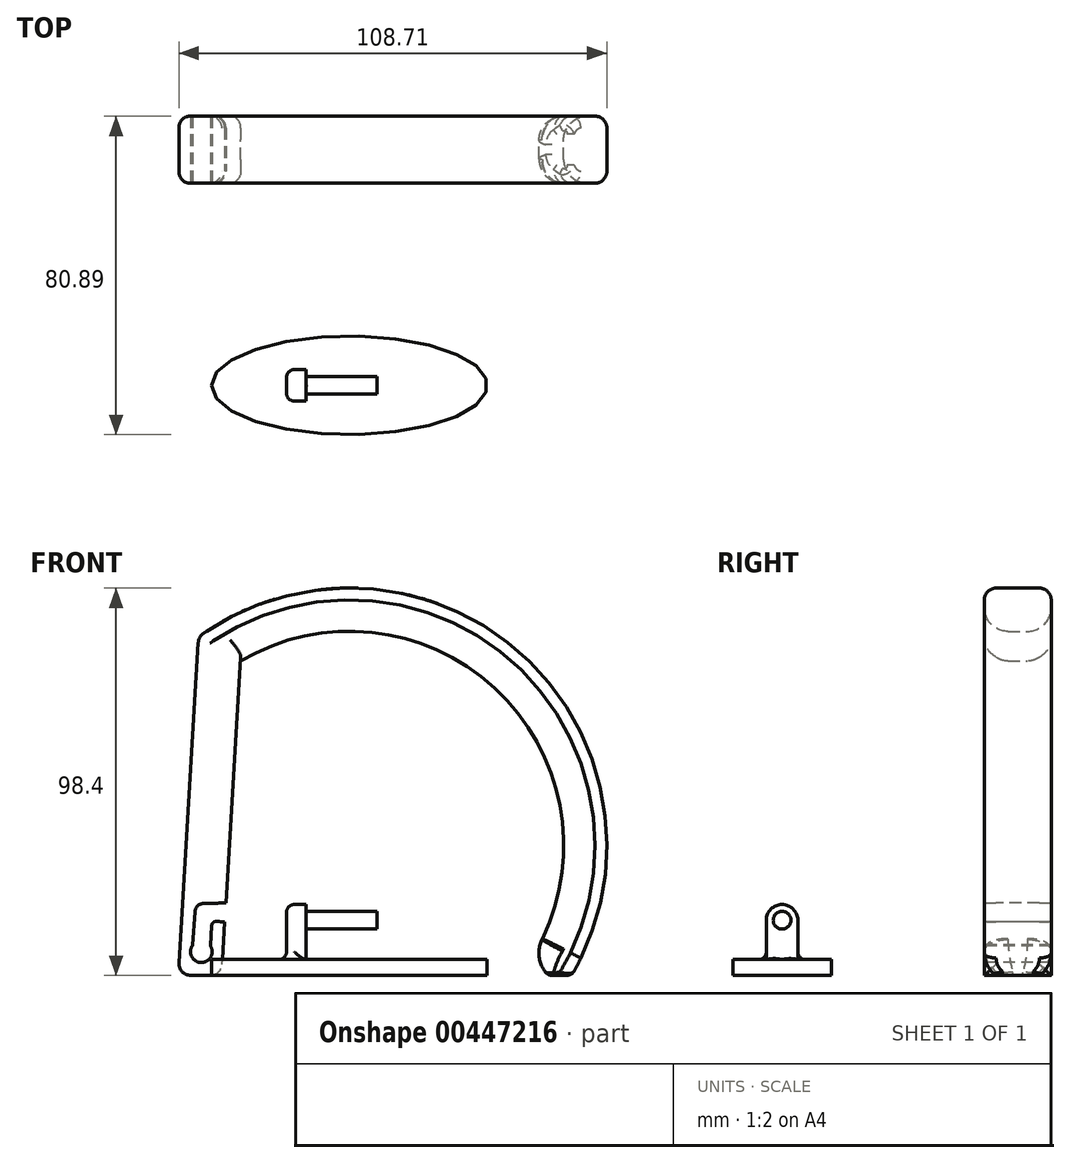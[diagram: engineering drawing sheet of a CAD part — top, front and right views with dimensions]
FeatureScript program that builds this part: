
annotation { "Feature Type Name" : "Feature", "Feature Type Description" : "" }
export const myFeature = defineFeature(function(context is Context, id is Id, definition is map)
    precondition{}
    {
        {
            var Q0;
            Q0=qCreatedBy(makeId("Front.planeOp"),FACE);
            var sketch = newSketch(context, id + "F0", { "sketchPlane" : qUnion([Q0])});
            skArc(sketch, "E0", {"start": v(50, 0) * mm, "mid": v(42.36, 75.36) * mm, "end": v(-33, 83) * mm});
            skLineSegment(sketch, "E1", {"start": v(-38, 0) * mm, "end": v(-33, 83) * mm});
            skArc(sketch, "E2", {"start": v(-33, 83) * mm, "mid": v(-58.69, 45.02) * mm, "end": v(-50, 0) * mm});
            skSolve(sketch);
        }
        {
            var Q0;
            Q0=qCreatedBy(makeId("Top.planeOp"),FACE);
            var sketch = newSketch(context, id + "F1", { "sketchPlane" : qUnion([Q0])});
            skLineSegment(sketch, "E3.bottom", {"start": v(-32.5, 8.5) * mm, "end": v(-43.5, 8.5) * mm});
            skLineSegment(sketch, "E3.top", {"start": v(-32.5, -8.5) * mm, "end": v(-43.5, -8.5) * mm});
            skLineSegment(sketch, "E3.left", {"start": v(-32.5, 8.5) * mm, "end": v(-32.5, -8.5) * mm});
            skLineSegment(sketch, "E3.right", {"start": v(-43.5, 8.5) * mm, "end": v(-43.5, -8.5) * mm});
            skPoint(sketch, "E3.middle", {"position": v(-38, 0) * mm});
            skSolve(sketch);
        }
        {
            var Q0;
            Q0=makeQuery(id+"F1.imprint","IMPRINT",FACE,{"disambiguationData":[TD([[makeQuery(id+"F1.imprint","IMPRINT",EDGE,{"derivedFrom":sQuery(id+"F1.wireOp",EDGE,"E3.bottom")}),1.0]])]});
            var Q1;
            Q1=sQuery(id+"F0.wireOp",EDGE,"E0");
            var Q2;
            Q2=sQuery(id+"F0.wireOp",EDGE,"E1");
            sweep(context, id + "F2", {"profiles" : qUnion([Q0]), "path" : qUnion([Q1, Q2])});
        }
        {
            var Q0;
            Q0=makeQuery(id+"F2.opSweep","SWEPT_FACE",FACE,{"disambiguationData":[OSD([sQuery(id+"F0.wireOp",EDGE,"E0"),sQuery(id+"F1.wireOp",EDGE,"E3.right")])]});
            var Q1;
            Q1=makeQuery(id+"F2.opSweep","SWEPT_FACE",FACE,{"disambiguationData":[OSD([sQuery(id+"F0.wireOp",EDGE,"E1"),sQuery(id+"F1.wireOp",EDGE,"E3.right")])]});
            var Q2;
            Q2=makeQuery(id+"F2.opSweep","SWEPT_EDGE",EDGE,{"disambiguationData":[OSD([sQuery(id+"F0.wireOp",EDGE,"E1"),sQuery(id+"F1.wireOp",EDGE,"E3.top"),sQuery(id+"F1.wireOp",EDGE,"E3.left")])]});
            var Q3;
            Q3=makeQuery(id+"F2.opSweep","SWEPT_EDGE",EDGE,{"disambiguationData":[OSD([sQuery(id+"F0.wireOp",EDGE,"E1"),sQuery(id+"F1.wireOp",EDGE,"E3.bottom"),sQuery(id+"F1.wireOp",EDGE,"E3.left")])]});
            var Q4;
            Q4=makeQuery(id+"F2.opSweep","CAP_EDGE",EDGE,{"disambiguationData":[OSD([sQuery(id+"F0.wireOp",VERTEX,"E1.start"),sQuery(id+"F1.wireOp",EDGE,"E3.left")])],"isStart":true});
            fillet(context, id + "F3", {"entities" : qUnion([Q0, Q1, Q2, Q3, Q4]), "radius" : 3 * mm, "tangentPropagation" : true, "allowEdgeOverflow" : false});
        }
        {
            var Q0;
            Q0=qCreatedBy(makeId("Front.planeOp"),FACE);
            var sketch = newSketch(context, id + "F4", { "sketchPlane" : qUnion([Q0])});
            skPoint(sketch, "E4", {"position": v(-37.64, 6) * mm});
            skPoint(sketch, "E5", {"position": v(-37.04, 16) * mm});
            skPoint(sketch, "E6", {"position": v(-27.04, 16) * mm});
            skCircle(sketch, "E7", {"center": v(-27.04, 16) * mm, "radius": 2.5 * mm});
            skCircle(sketch, "E8", {"center": v(-37.04, 16) * mm, "radius": 2.25 * mm});
            skCircle(sketch, "E9", {"center": v(-37.64, 6) * mm, "radius": 2.25 * mm});
            skLineSegment(sketch, "E10", {"start": v(-35.4, 5.86) * mm, "end": v(-34.8, 15.86) * mm});
            skLineSegment(sketch, "E11", {"start": v(-39.88, 6.14) * mm, "end": v(-39.28, 16.14) * mm});
            skLineSegment(sketch, "E12", {"start": v(-27.1, 18.5) * mm, "end": v(-37.1, 18.25) * mm});
            skLineSegment(sketch, "E13", {"start": v(-27.1, 13.5) * mm, "end": v(-37.1, 13.75) * mm});
            skCircle(sketch, "E14", {"center": v(-37.64, 6) * mm, "radius": 2.75 * mm});
            skSolve(sketch);
        }
        {
            var Q0;
            {var subQ0=sQuery(id+"F4.wireOp",EDGE,"E7");var subQ1=makeQuery(id+"F4.imprint","INTERSECT",VERTEX,{"derivedFrom":[subQ0,sQuery(id+"F4.wireOp",EDGE,"E12")]});Q0=makeQuery(id+"F4.imprint","IMPRINT",FACE,{"disambiguationData":[TD([[makeQuery(id+"F4.imprint","IMPRINT",EDGE,{"disambiguationData":[TD([[subQ1,-1.0]])],"derivedFrom":subQ0}),1.0]])]});}
            var Q1;
            {var subQ0=sQuery(id+"F4.wireOp",EDGE,"E12");Q1=makeQuery(id+"F4.imprint","IMPRINT",FACE,{"disambiguationData":[TD([[makeQuery(id+"F4.imprint","IMPRINT",EDGE,{"derivedFrom":subQ0}),1.0]])]});}
            var Q2;
            {var subQ0=sQuery(id+"F4.wireOp",EDGE,"E8");var subQ1=makeQuery(id+"F4.imprint","INTERSECT",VERTEX,{"derivedFrom":[subQ0,sQuery(id+"F4.wireOp",EDGE,"E10")]});Q2=makeQuery(id+"F4.imprint","IMPRINT",FACE,{"disambiguationData":[TD([[makeQuery(id+"F4.imprint","IMPRINT",EDGE,{"disambiguationData":[TD([[subQ1,-1.0]])],"derivedFrom":subQ0}),1.0]])]});}
            var Q3;
            {var subQ1=sQuery(id+"F4.wireOp",EDGE,"E8");var subQ5=sQuery(id+"F4.wireOp",EDGE,"E11");var subQ6=makeQuery(id+"F4.imprint","INTERSECT",VERTEX,{"derivedFrom":[subQ1,subQ5]});Q3=makeQuery(id+"F4.imprint","IMPRINT",FACE,{"disambiguationData":[TD([[makeQuery(id+"F4.imprint","IMPRINT",EDGE,{"disambiguationData":[TD([[subQ6,-1.0]])],"derivedFrom":subQ1}),-1.0]])]});}
            var Q4;
            {var subQ0=sQuery(id+"F4.wireOp",EDGE,"E10");var subQ1=sQuery(id+"F4.wireOp",EDGE,"E8");var subQ2=makeQuery(id+"F4.imprint","INTERSECT",VERTEX,{"derivedFrom":[subQ1,subQ0]});Q4=makeQuery(id+"F4.imprint","IMPRINT",FACE,{"disambiguationData":[TD([[makeQuery(id+"F4.imprint","IMPRINT",EDGE,{"disambiguationData":[TD([[subQ2,1.0]])],"derivedFrom":subQ1}),-1.0]])]});}
            var Q5;
            {var subQ0=sQuery(id+"F4.wireOp",EDGE,"E10");var subQ1=sQuery(id+"F4.wireOp",EDGE,"E9");var subQ2=makeQuery(id+"F4.imprint","INTERSECT",VERTEX,{"derivedFrom":[subQ1,subQ0]});Q5=makeQuery(id+"F4.imprint","IMPRINT",FACE,{"disambiguationData":[TD([[makeQuery(id+"F4.imprint","IMPRINT",EDGE,{"disambiguationData":[TD([[subQ2,-1.0]])],"derivedFrom":subQ1}),-1.0]])]});}
            var Q6;
            {var subQ0=sQuery(id+"F4.wireOp",EDGE,"E10");var subQ1=sQuery(id+"F4.wireOp",EDGE,"E9");var subQ2=makeQuery(id+"F4.imprint","INTERSECT",VERTEX,{"derivedFrom":[subQ1,subQ0]});Q6=makeQuery(id+"F4.imprint","IMPRINT",FACE,{"disambiguationData":[TD([[makeQuery(id+"F4.imprint","IMPRINT",EDGE,{"disambiguationData":[TD([[subQ2,1.0]])],"derivedFrom":subQ1}),-1.0]])]});}
            var Q7;
            {var subQ0=sQuery(id+"F4.wireOp",EDGE,"E9");var subQ1=makeQuery(id+"F4.imprint","INTERSECT",VERTEX,{"derivedFrom":[subQ0,sQuery(id+"F4.wireOp",EDGE,"E10")]});Q7=makeQuery(id+"F4.imprint","IMPRINT",FACE,{"disambiguationData":[TD([[makeQuery(id+"F4.imprint","IMPRINT",EDGE,{"disambiguationData":[TD([[subQ1,-1.0]])],"derivedFrom":subQ0}),1.0]])]});}
            extrude(context, id + "F5", {"entities" : qUnion([Q0, Q1, Q2, Q3, Q4, Q5, Q6, Q7]), "operationType" : NewBodyOperationType.REMOVE, "oppositeDirection" : true, "depth" : 12 * mm, "hasSecondDirection" : true, "secondDirectionOppositeDirection" : false, "secondDirectionDepth" : 12 * mm, "offsetDistance" : 25 * mm});
        }
        {
            var Q0;
            Q0=makeQuery(id+"F5.boolean.opBoolean","COPY",EDGE,{"derivedFrom":makeQuery(id+"F5.opExtrude","SWEPT_EDGE",EDGE,{"disambiguationData":[OSD([sQuery(id+"F4.wireOp",EDGE,"E10"),sQuery(id+"F4.wireOp",EDGE,"E13")])]})});
            fillet(context, id + "F6", {"entities" : qUnion([Q0]), "radius" : 1 * mm, "tangentPropagation" : true, "allowEdgeOverflow" : false});
        }
        {
            var Q0;
            {var subQ0=sQuery(id+"F1.wireOp",EDGE,"E3.left");var subQ1=sQuery(id+"F1.wireOp",EDGE,"E3.bottom");var subQ2=sQuery(id+"F0.wireOp",EDGE,"E0");Q0=makeQuery(id+"F5.boolean.opBoolean","SPLIT",EDGE,{"disambiguationData":[TD([makeQuery(id+"F5.opExtrude","SWEPT_FACE",FACE,{"disambiguationData":[OSD([sQuery(id+"F4.wireOp",EDGE,"E12")])]})])],"derivedFrom":makeQuery(id+"F2.opSweep","SWEPT_EDGE",EDGE,{"disambiguationData":[OSD([subQ2,subQ1,subQ0])]})});}
            var Q1;
            {var subQ0=sQuery(id+"F1.wireOp",EDGE,"E3.left");var subQ1=sQuery(id+"F1.wireOp",EDGE,"E3.top");var subQ2=sQuery(id+"F0.wireOp",EDGE,"E0");Q1=makeQuery(id+"F5.boolean.opBoolean","SPLIT",EDGE,{"disambiguationData":[TD([makeQuery(id+"F5.opExtrude","SWEPT_FACE",FACE,{"disambiguationData":[OSD([sQuery(id+"F4.wireOp",EDGE,"E12")])]})])],"derivedFrom":makeQuery(id+"F2.opSweep","SWEPT_EDGE",EDGE,{"disambiguationData":[OSD([subQ2,subQ1,subQ0])]})});}
            var Q2;
            Q2=makeQuery(id+"F2.opSweep","CAP_EDGE",EDGE,{"disambiguationData":[OSD([sQuery(id+"F0.wireOp",VERTEX,"E1.start"),sQuery(id+"F1.wireOp",EDGE,"E3.left")])],"isStart":true});
            fillet(context, id + "F7", {"entities" : qUnion([Q0, Q1, Q2]), "radius" : 6 * mm, "tangentPropagation" : true, "allowEdgeOverflow" : false});
        }
        {
            var Q0;
            Q0=makeQuery(id+"F2.opSweep","CAP_EDGE",EDGE,{"disambiguationData":[OSD([sQuery(id+"F0.wireOp",VERTEX,"E0.start"),sQuery(id+"F1.wireOp",EDGE,"E3.left")])],"isStart":false});
            fillet(context, id + "F8", {"entities" : qUnion([Q0]), "radius" : 8 * mm, "tangentPropagation" : true, "allowEdgeOverflow" : false});
        }
        {
            var Q0;
            Q0=qCreatedBy(makeId("Top.planeOp"),FACE);
            var sketch = newSketch(context, id + "F9", { "sketchPlane" : qUnion([Q0])});
            skLineSegment(sketch, "E15.bottom", {"start": v(68.74, 41) * mm, "end": v(27.5, 41) * mm});
            skLineSegment(sketch, "E15.top", {"start": v(68.74, -30.42) * mm, "end": v(27.5, -30.42) * mm});
            skLineSegment(sketch, "E15.left", {"start": v(68.74, 41) * mm, "end": v(68.74, -30.42) * mm});
            skLineSegment(sketch, "E15.right", {"start": v(27.5, 41) * mm, "end": v(27.5, -30.42) * mm});
            skSolve(sketch);
        }
        {
            var Q0;
            Q0=makeQuery(id+"F9.imprint","IMPRINT",FACE,{"disambiguationData":[TD([[makeQuery(id+"F9.imprint","IMPRINT",EDGE,{"derivedFrom":sQuery(id+"F9.wireOp",EDGE,"E15.bottom")}),1.0]])]});
            extrude(context, id + "F10", {"entities" : qUnion([Q0]), "operationType" : NewBodyOperationType.REMOVE, "oppositeDirection" : true, "depth" : 25 * mm});
        }
        {
            var Q0;
            Q0=makeQuery(id+"F10.boolean.opBoolean","INTERSECT",EDGE,{"derivedFrom":[makeQuery(id+"F2.opSweep","SWEPT_FACE",FACE,{"disambiguationData":[OSD([sQuery(id+"F0.wireOp",EDGE,"E0"),sQuery(id+"F1.wireOp",EDGE,"E3.right")])]}),makeQuery(id+"F10.opExtrude","CAP_FACE",FACE,{"disambiguationData":[OSD([sQuery(id+"F9.wireOp",EDGE,"E15.bottom"),sQuery(id+"F9.wireOp",EDGE,"E15.top"),sQuery(id+"F9.wireOp",EDGE,"E15.left"),sQuery(id+"F9.wireOp",EDGE,"E15.right")])],"isStart":true})]});
            var Q1;
            Q1=makeQuery(id+"F10.boolean.opBoolean","INTERSECT",EDGE,{"derivedFrom":[makeQuery(id+"F2.opSweep","CAP_FACE",FACE,{"disambiguationData":[OSD([sQuery(id+"F0.wireOp",VERTEX,"E0.start"),sQuery(id+"F1.wireOp",EDGE,"E3.bottom"),sQuery(id+"F1.wireOp",EDGE,"E3.top"),sQuery(id+"F1.wireOp",EDGE,"E3.left"),sQuery(id+"F1.wireOp",EDGE,"E3.right")])],"isStart":false}),makeQuery(id+"F10.opExtrude","CAP_FACE",FACE,{"disambiguationData":[OSD([sQuery(id+"F9.wireOp",EDGE,"E15.bottom"),sQuery(id+"F9.wireOp",EDGE,"E15.top"),sQuery(id+"F9.wireOp",EDGE,"E15.left"),sQuery(id+"F9.wireOp",EDGE,"E15.right")])],"isStart":true})]});
            fillet(context, id + "F11", {"entities" : qUnion([Q0, Q1]), "radius" : 2 * mm, "tangentPropagation" : true, "allowEdgeOverflow" : false});
        }
        {
            var Q0;
            Q0=qCreatedBy(makeId("Top.planeOp"),FACE);
            var sketch = newSketch(context, id + "F12", { "sketchPlane" : qUnion([Q0])});
            skEllipse(sketch, "E16", {"center": v(0, -59.9) * mm, "majorRadius": 35 * mm, "minorRadius": 12.5 * mm, "majorAxis": v(1, 0)});
            skPoint(sketch, "E17", {"position": v(27, -59.9) * mm});
            skPoint(sketch, "E18", {"position": v(-27, -59.9) * mm});
            skSolve(sketch);
        }
        {
            var Q0;
            Q0=makeQuery(id+"F12.imprint","IMPRINT",FACE,{"disambiguationData":[TD([[makeQuery(id+"F12.imprint","IMPRINT",EDGE,{"derivedFrom":sQuery(id+"F12.wireOp",EDGE,"E16")}),1.0]])]});
            extrude(context, id + "F13", {"entities" : qUnion([Q0]), "depth" : 4 * mm});
        }
        {
            var Q0;
            Q0=qCreatedBy(makeId("Right.planeOp"),FACE);
            cPlane(context, id + "F14", {"entities" : qUnion([Q0]), "cplaneType" : CPlaneType.OFFSET, "offset" : 11 * mm, "width" : 150 * mm, "height" : 150 * mm});
        }
        {
            var Q0;
            Q0=qCreatedBy(id+"F14.planeOp",FACE);
            var sketch = newSketch(context, id + "F15", { "sketchPlane" : qUnion([Q0])});
            skLineSegment(sketch, "E19.bottom", {"start": v(-63.9, 0) * mm, "end": v(-55.9, 0) * mm});
            skLineSegment(sketch, "E19.top", {"start": v(-63.9, 18) * mm, "end": v(-55.9, 18) * mm});
            skLineSegment(sketch, "E19.left", {"start": v(-63.9, 0) * mm, "end": v(-63.9, 18) * mm});
            skLineSegment(sketch, "E19.right", {"start": v(-55.9, 0) * mm, "end": v(-55.9, 18) * mm});
            skCircle(sketch, "E20", {"center": v(-59.9, 14) * mm, "radius": 2.25 * mm});
            skSolve(sketch);
        }
        {
            var Q0;
            Q0=makeQuery(id+"F15.imprint","IMPRINT",FACE,{"disambiguationData":[TD([[makeQuery(id+"F15.imprint","IMPRINT",EDGE,{"derivedFrom":sQuery(id+"F15.wireOp",EDGE,"E19.bottom")}),1.0]])]});
            var Q1;
            Q1=makeQuery(id+"F15.imprint","IMPRINT",FACE,{"disambiguationData":[TD([[makeQuery(id+"F15.imprint","IMPRINT",EDGE,{"derivedFrom":sQuery(id+"F15.wireOp",EDGE,"E20")}),1.0]])]});
            extrude(context, id + "F16", {"entities" : qUnion([Q0, Q1]), "operationType" : NewBodyOperationType.ADD, "depth" : 5 * mm});
        }
        {
            var Q0;
            Q0=makeQuery(id+"F15.imprint","IMPRINT",FACE,{"disambiguationData":[TD([[makeQuery(id+"F15.imprint","IMPRINT",EDGE,{"derivedFrom":sQuery(id+"F15.wireOp",EDGE,"E20")}),1.0]])]});
            var Q1;
            Q1=sQuery(id+"F15.wireOp",EDGE,"E20");
            extrude(context, id + "F17", {"entities" : qUnion([Q0]), "operationType" : NewBodyOperationType.ADD, "surfaceEntities" : qUnion([Q1]), "oppositeDirection" : true, "depth" : 18 * mm});
        }
        {
            var Q0;
            Q0=makeQuery(id+"F16.opExtrude","SWEPT_EDGE",EDGE,{"disambiguationData":[OSD([sQuery(id+"F15.wireOp",EDGE,"E19.top"),sQuery(id+"F15.wireOp",EDGE,"E19.left")])]});
            var Q1;
            Q1=makeQuery(id+"F16.opExtrude","SWEPT_EDGE",EDGE,{"disambiguationData":[OSD([sQuery(id+"F15.wireOp",EDGE,"E19.top"),sQuery(id+"F15.wireOp",EDGE,"E19.right")])]});
            fillet(context, id + "F18", {"entities" : qUnion([Q0, Q1]), "radius" : 4 * mm, "tangentPropagation" : true, "allowEdgeOverflow" : false});
        }
        {
            var Q0;
            Q0=makeQuery(id+"F16.opExtrude","CAP_FACE",FACE,{"disambiguationData":[OSD([sQuery(id+"F15.wireOp",EDGE,"E19.bottom"),sQuery(id+"F15.wireOp",EDGE,"E19.top"),sQuery(id+"F15.wireOp",EDGE,"E19.left"),sQuery(id+"F15.wireOp",EDGE,"E19.right")])],"isStart":false});
            fillet(context, id + "F19", {"entities" : qUnion([Q0]), "radius" : 2 * mm, "tangentPropagation" : true, "allowEdgeOverflow" : false});
        }
        {
            var Q0;
            Q0=makeQuery(id+"F13.opExtrude","SWEPT_BODY",BODY,{"disambiguationData":[OSD([sQuery(id+"F12.wireOp",EDGE,"E16")])]});
            var Q1;
            Q1=qCreatedBy(makeId("Right.planeOp"),FACE);
            mirror(context, id + "F20", {"operationType" : NewBodyOperationType.ADD, "entities" : qUnion([Q0]), "mirrorPlane" : qUnion([Q1])});
        }
        {
            var Q0;
            Q0=sQuery(id+"F12.wireOp",VERTEX,"E17");
            var Q1;
            Q1=sQuery(id+"F12.wireOp",VERTEX,"E18");
            var Q2;
            Q2=makeQuery(id+"F13.opExtrude","SWEPT_BODY",BODY,{"disambiguationData":[OSD([sQuery(id+"F12.wireOp",EDGE,"E16")])]});
            hole(context, id + "F21", {"style" : HoleStyle.SIMPLE, "endStyle" : HoleEndStyle.THROUGH, "oppositeDirection" : true, "holeDiameter" : 4 * mm, "isTappedThrough" : true, "tappedDepth" : 12 * mm, "tapClearance" : 3, "locations" : qUnion([Q0, Q1]), "scope" : qUnion([Q2])});
        }
        {
            var Q0;
            Q0=makeQuery(id+"F13.opExtrude","SWEPT_BODY",BODY,{"disambiguationData":[OSD([sQuery(id+"F12.wireOp",EDGE,"E16")])]});
            deleteBodies(context, id + "F22", {"entities" : qUnion([Q0])});
        }
    });
